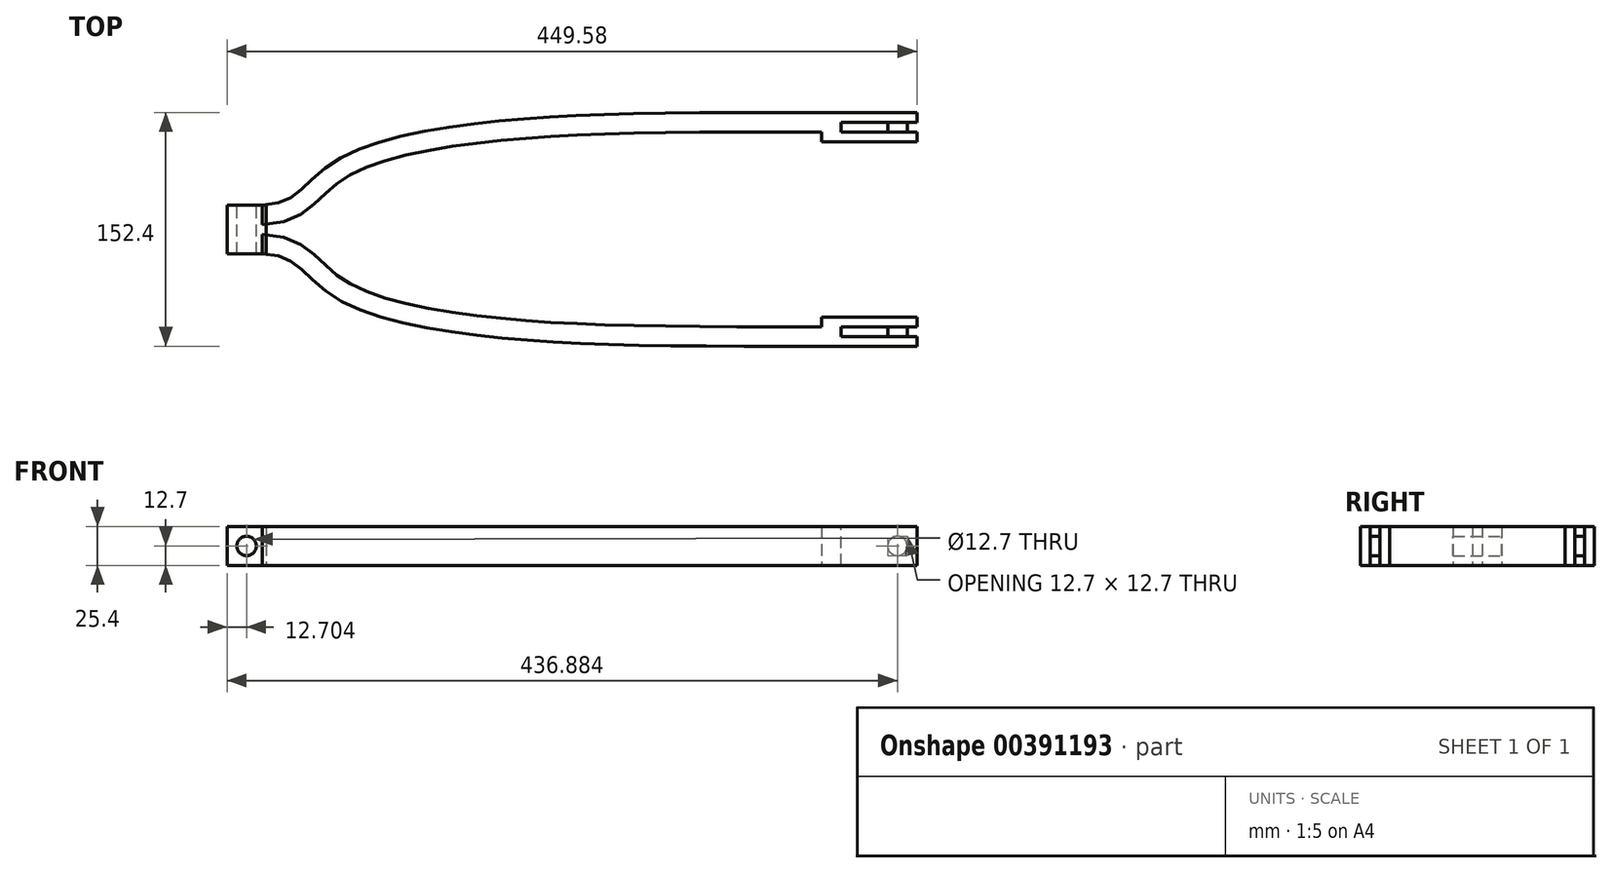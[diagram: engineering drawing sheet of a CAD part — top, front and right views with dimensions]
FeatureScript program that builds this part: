
annotation { "Feature Type Name" : "Feature", "Feature Type Description" : "" }
export const myFeature = defineFeature(function(context is Context, id is Id, definition is map)
    precondition{}
    {
        {
            var Q0;
            Q0=qCreatedBy(makeId("Top.planeOp"),FACE);
            var sketch = newSketch(context, id + "F0", { "sketchPlane" : qUnion([Q0])});
            skLineSegment(sketch, "E0", {"start": v(-147.55, 0) * mm, "end": v(274.1, 0) * mm, "construction": true});
            skFitSpline(sketch, "E1", {"points": [v(-147.55, -9.53) * mm, v(-100.59, -36.49) * mm, v(0, -63.5) * mm, v(223.3, -69.85) * mm], "startDerivative": vector(326.66, -0.96) * mm, "endDerivative": vector(713.6, 0) * mm});
            skLineSegment(sketch, "E2", {"start": v(-147.55, -185.95) * mm, "end": v(-147.55, 189.82) * mm, "construction": true});
            skFitSpline(sketch, "E3.MirrorCS", {"points": [v(-147.55, 9.53) * mm, v(-100.59, 36.49) * mm, v(0, 63.5) * mm, v(223.3, 69.85) * mm], "startDerivative": vector(326.66, 0.96) * mm, "endDerivative": vector(713.6, 0) * mm});
            skLineSegment(sketch, "E4", {"start": v(223.3, -69.85) * mm, "end": v(223.3, 69.85) * mm, "construction": true});
            skLineSegment(sketch, "E5", {"start": v(223.3, 69.85) * mm, "end": v(223.3, 69.85) * mm});
            skLineSegment(sketch, "E6", {"start": v(279.17, -108.03) * mm, "end": v(279.17, 69.85) * mm, "construction": true});
            skLineSegment(sketch, "E7", {"start": v(279.17, 57.15) * mm, "end": v(223.3, 57.15) * mm});
            skLineSegment(sketch, "E8", {"start": v(279.17, -57.15) * mm, "end": v(223.3, -57.15) * mm});
            skLineSegment(sketch, "E9", {"start": v(223.3, 69.85) * mm, "end": v(279.17, 69.85) * mm});
            skLineSegment(sketch, "E10", {"start": v(223.3, -69.85) * mm, "end": v(279.17, -69.85) * mm});
            skSolve(sketch);
        }
        {
            var Q0;
            Q0=sQuery(id+"F0.wireOp",VERTEX,"E3.MirrorCS.0.internal");
            var Q1;
            Q1=qCreatedBy(makeId("Right.planeOp"),FACE);
            cPlane(context, id + "F1", {"entities" : qUnion([Q0, Q1]), "cplaneType" : CPlaneType.PLANE_POINT, "offset" : 25.4 * mm, "width" : 152.4 * mm, "height" : 152.4 * mm});
        }
        {
            var Q0;
            Q0=qCreatedBy(id+"F1.planeOp",FACE);
            var sketch = newSketch(context, id + "F2", { "sketchPlane" : qUnion([Q0])});
            skLineSegment(sketch, "E11.bottom", {"start": v(15.88, 12.7) * mm, "end": v(3.18, 12.7) * mm});
            skLineSegment(sketch, "E11.top", {"start": v(15.88, -12.7) * mm, "end": v(3.18, -12.7) * mm});
            skLineSegment(sketch, "E11.left", {"start": v(15.88, 12.7) * mm, "end": v(15.88, -12.7) * mm});
            skLineSegment(sketch, "E11.right", {"start": v(3.18, 12.7) * mm, "end": v(3.18, -12.7) * mm});
            skPoint(sketch, "E11.middle", {"position": v(9.53, 0) * mm});
            skLineSegment(sketch, "E12.bottom", {"start": v(-3.18, 12.7) * mm, "end": v(-15.88, 12.7) * mm});
            skLineSegment(sketch, "E12.top", {"start": v(-3.18, -12.7) * mm, "end": v(-15.88, -12.7) * mm});
            skLineSegment(sketch, "E12.left", {"start": v(-3.18, 12.7) * mm, "end": v(-3.17, -12.7) * mm});
            skLineSegment(sketch, "E12.right", {"start": v(-15.88, 12.7) * mm, "end": v(-15.88, -12.7) * mm});
            skPoint(sketch, "E12.middle", {"position": v(-9.52, 0) * mm});
            skSolve(sketch);
        }
        {
            var Q0;
            Q0=makeQuery(id+"F2.imprint","IMPRINT",FACE,{"disambiguationData":[TD([[makeQuery(id+"F2.imprint","IMPRINT",EDGE,{"derivedFrom":sQuery(id+"F2.wireOp",EDGE,"E12.bottom")}),1.0]])]});
            var Q1;
            Q1=sQuery(id+"F0.wireOp",EDGE,"E1");
            sweep(context, id + "F3", {"profiles" : qUnion([Q0]), "path" : qUnion([Q1])});
        }
        {
            var Q0;
            Q0=makeQuery(id+"F2.imprint","IMPRINT",FACE,{"disambiguationData":[TD([[makeQuery(id+"F2.imprint","IMPRINT",EDGE,{"derivedFrom":sQuery(id+"F2.wireOp",EDGE,"E11.bottom")}),1.0]])]});
            var Q1;
            Q1=sQuery(id+"F0.wireOp",EDGE,"E3.MirrorCS");
            sweep(context, id + "F4", {"profiles" : qUnion([Q0]), "path" : qUnion([Q1])});
        }
        {
            var Q0;
            Q0=sQuery(id+"F0.wireOp",VERTEX,"E8.end");
            var Q1;
            Q1=qCreatedBy(makeId("Right.planeOp"),FACE);
            cPlane(context, id + "F5", {"entities" : qUnion([Q0, Q1]), "cplaneType" : CPlaneType.PLANE_POINT, "offset" : 25.4 * mm, "width" : 152.4 * mm, "height" : 152.4 * mm});
        }
        {
            var Q0;
            Q0=qCreatedBy(id+"F5.planeOp",FACE);
            var sketch = newSketch(context, id + "F6", { "sketchPlane" : qUnion([Q0])});
            skLineSegment(sketch, "E13.bottom", {"start": v(-63.5, -12.7) * mm, "end": v(-57.15, -12.7) * mm});
            skLineSegment(sketch, "E13.top", {"start": v(-63.5, 12.7) * mm, "end": v(-57.15, 12.7) * mm});
            skLineSegment(sketch, "E13.left", {"start": v(-63.5, -12.7) * mm, "end": v(-63.5, 12.7) * mm});
            skLineSegment(sketch, "E13.right", {"start": v(-57.15, -12.7) * mm, "end": v(-57.15, 12.7) * mm});
            skLineSegment(sketch, "E14.bottom", {"start": v(-76.2, 12.7) * mm, "end": v(-69.85, 12.7) * mm});
            skLineSegment(sketch, "E14.top", {"start": v(-76.2, -12.7) * mm, "end": v(-69.85, -12.7) * mm});
            skLineSegment(sketch, "E14.left", {"start": v(-76.2, 12.7) * mm, "end": v(-76.2, -12.7) * mm});
            skLineSegment(sketch, "E14.right", {"start": v(-69.85, 12.7) * mm, "end": v(-69.85, -12.7) * mm});
            skLineSegment(sketch, "E15.bottom", {"start": v(57.15, 12.7) * mm, "end": v(63.5, 12.7) * mm});
            skLineSegment(sketch, "E15.top", {"start": v(57.15, -12.7) * mm, "end": v(63.5, -12.7) * mm});
            skLineSegment(sketch, "E15.left", {"start": v(57.15, 12.7) * mm, "end": v(57.15, -12.7) * mm});
            skLineSegment(sketch, "E15.right", {"start": v(63.5, 12.7) * mm, "end": v(63.5, -12.7) * mm});
            skLineSegment(sketch, "E16.bottom", {"start": v(69.85, -12.7) * mm, "end": v(76.2, -12.7) * mm});
            skLineSegment(sketch, "E16.top", {"start": v(69.85, 12.7) * mm, "end": v(76.2, 12.7) * mm});
            skLineSegment(sketch, "E16.left", {"start": v(69.85, -12.7) * mm, "end": v(69.85, 12.7) * mm});
            skLineSegment(sketch, "E16.right", {"start": v(76.2, -12.7) * mm, "end": v(76.2, 12.7) * mm});
            skSolve(sketch);
        }
        {
            var Q0;
            Q0=makeQuery(id+"F6.imprint","IMPRINT",FACE,{"disambiguationData":[TD([[makeQuery(id+"F6.imprint","IMPRINT",EDGE,{"derivedFrom":sQuery(id+"F6.wireOp",EDGE,"E13.bottom")}),1.0]])]});
            var Q1;
            Q1=sQuery(id+"F0.wireOp",EDGE,"E8");
            sweep(context, id + "F7", {"profiles" : qUnion([Q0]), "path" : qUnion([Q1])});
        }
        {
            var Q0;
            Q0=makeQuery(id+"F6.imprint","IMPRINT",FACE,{"disambiguationData":[TD([[makeQuery(id+"F6.imprint","IMPRINT",EDGE,{"derivedFrom":sQuery(id+"F6.wireOp",EDGE,"E14.bottom")}),-1.0]])]});
            var Q1;
            Q1=sQuery(id+"F0.wireOp",EDGE,"E10");
            sweep(context, id + "F8", {"profiles" : qUnion([Q0]), "path" : qUnion([Q1])});
        }
        {
            var Q0;
            Q0=makeQuery(id+"F6.imprint","IMPRINT",FACE,{"disambiguationData":[TD([[makeQuery(id+"F6.imprint","IMPRINT",EDGE,{"derivedFrom":sQuery(id+"F6.wireOp",EDGE,"E16.bottom")}),1.0]])]});
            var Q1;
            Q1=sQuery(id+"F0.wireOp",EDGE,"E9");
            sweep(context, id + "F9", {"profiles" : qUnion([Q0]), "path" : qUnion([Q1])});
        }
        {
            var Q0;
            Q0=makeQuery(id+"F6.imprint","IMPRINT",FACE,{"disambiguationData":[TD([[makeQuery(id+"F6.imprint","IMPRINT",EDGE,{"derivedFrom":sQuery(id+"F6.wireOp",EDGE,"E15.bottom")}),-1.0]])]});
            var Q1;
            Q1=sQuery(id+"F0.wireOp",EDGE,"E7");
            sweep(context, id + "F10", {"profiles" : qUnion([Q0]), "path" : qUnion([Q1])});
        }
        {
            var Q0;
            Q0=makeQuery(id+"F4.opSweep","CAP_VERTEX",VERTEX,{"disambiguationData":[OSD([sQuery(id+"F0.wireOp",EDGE,"E3.MirrorCS"),sQuery(id+"F2.wireOp",EDGE,"E11.bottom"),sQuery(id+"F2.wireOp",EDGE,"E11.left")])],"isStart":false});
            var Q1;
            Q1=qCreatedBy(makeId("Front.planeOp"),FACE);
            cPlane(context, id + "F11", {"entities" : qUnion([Q0, Q1]), "cplaneType" : CPlaneType.PLANE_POINT, "offset" : 25.4 * mm, "width" : 152.4 * mm, "height" : 152.4 * mm});
        }
        {
            var Q0;
            Q0=qCreatedBy(id+"F11.planeOp",FACE);
            var sketch = newSketch(context, id + "F12", { "sketchPlane" : qUnion([Q0])});
            skLineSegment(sketch, "E17.bottom", {"start": v(216.94, 12.7) * mm, "end": v(223.3, 12.7) * mm});
            skLineSegment(sketch, "E17.top", {"start": v(216.94, -12.7) * mm, "end": v(229.64, -12.7) * mm});
            skLineSegment(sketch, "E17.left", {"start": v(216.94, 12.7) * mm, "end": v(216.94, -12.7) * mm});
            skLineSegment(sketch, "E17.right", {"start": v(229.64, 12.7) * mm, "end": v(229.64, -12.7) * mm});
            skLineSegment(sketch, "E18", {"start": v(223.3, 12.7) * mm, "end": v(229.64, 12.7) * mm});
            skSolve(sketch);
        }
        {
            var Q0;
            Q0=makeQuery(id+"F12.imprint","IMPRINT",FACE,{"disambiguationData":[TD([[makeQuery(id+"F12.imprint","IMPRINT",EDGE,{"derivedFrom":sQuery(id+"F12.wireOp",EDGE,"E17.bottom")}),-1.0]])]});
            extrude(context, id + "F13", {"entities" : qUnion([Q0]), "depth" : 19.05 * mm});
        }
        {
            var Q0;
            Q0=makeQuery(id+"F3.opSweep","CAP_VERTEX",VERTEX,{"disambiguationData":[OSD([sQuery(id+"F0.wireOp",EDGE,"E1"),sQuery(id+"F2.wireOp",EDGE,"E12.bottom"),sQuery(id+"F2.wireOp",EDGE,"E12.right")])],"isStart":false});
            var Q1;
            Q1=qCreatedBy(makeId("Front.planeOp"),FACE);
            cPlane(context, id + "F14", {"entities" : qUnion([Q0, Q1]), "cplaneType" : CPlaneType.PLANE_POINT, "offset" : 25.4 * mm, "width" : 152.4 * mm, "height" : 152.4 * mm});
        }
        {
            var Q0;
            Q0=qCreatedBy(id+"F14.planeOp",FACE);
            var sketch = newSketch(context, id + "F15", { "sketchPlane" : qUnion([Q0])});
            skLineSegment(sketch, "E19.bottom", {"start": v(216.94, 12.7) * mm, "end": v(223.3, 12.7) * mm});
            skLineSegment(sketch, "E19.top", {"start": v(216.94, -12.7) * mm, "end": v(229.64, -12.7) * mm});
            skLineSegment(sketch, "E19.left", {"start": v(216.94, 12.7) * mm, "end": v(216.94, -12.7) * mm});
            skLineSegment(sketch, "E19.right", {"start": v(229.64, 12.7) * mm, "end": v(229.64, -12.7) * mm});
            skLineSegment(sketch, "E20", {"start": v(223.3, 12.7) * mm, "end": v(229.64, 12.7) * mm});
            skSolve(sketch);
        }
        {
            var Q0;
            Q0=makeQuery(id+"F15.imprint","IMPRINT",FACE,{"disambiguationData":[TD([[makeQuery(id+"F15.imprint","IMPRINT",EDGE,{"derivedFrom":sQuery(id+"F15.wireOp",EDGE,"E19.bottom")}),-1.0]])]});
            extrude(context, id + "F16", {"entities" : qUnion([Q0]), "oppositeDirection" : true, "depth" : 19.05 * mm});
        }
        {
            var Q0;
            Q0=makeQuery(id+"F3.opSweep","SWEPT_BODY",BODY,{"disambiguationData":[OSD([sQuery(id+"F0.wireOp",EDGE,"E1"),sQuery(id+"F2.wireOp",EDGE,"E12.bottom"),sQuery(id+"F2.wireOp",EDGE,"E12.top"),sQuery(id+"F2.wireOp",EDGE,"E12.left"),sQuery(id+"F2.wireOp",EDGE,"E12.right")])]});
            var Q1;
            Q1=makeQuery(id+"F16.opExtrude","SWEPT_BODY",BODY,{"disambiguationData":[OSD([sQuery(id+"F15.wireOp",EDGE,"E19.bottom"),sQuery(id+"F15.wireOp",EDGE,"E19.top"),sQuery(id+"F15.wireOp",EDGE,"E19.left"),sQuery(id+"F15.wireOp",EDGE,"E19.right"),sQuery(id+"F15.wireOp",EDGE,"E20")])]});
            var Q2;
            Q2=makeQuery(id+"F8.opSweep","SWEPT_BODY",BODY,{"disambiguationData":[OSD([sQuery(id+"F0.wireOp",EDGE,"E10"),sQuery(id+"F6.wireOp",EDGE,"E14.bottom"),sQuery(id+"F6.wireOp",EDGE,"E14.top"),sQuery(id+"F6.wireOp",EDGE,"E14.left"),sQuery(id+"F6.wireOp",EDGE,"E14.right")])]});
            var Q3;
            Q3=makeQuery(id+"F7.opSweep","SWEPT_BODY",BODY,{"disambiguationData":[OSD([sQuery(id+"F0.wireOp",EDGE,"E8"),sQuery(id+"F6.wireOp",EDGE,"E13.bottom"),sQuery(id+"F6.wireOp",EDGE,"E13.top"),sQuery(id+"F6.wireOp",EDGE,"E13.left"),sQuery(id+"F6.wireOp",EDGE,"E13.right")])]});
            booleanBodies(context, id + "F17", {"operationType" : BooleanOperationType.UNION, "tools" : qUnion([Q0, Q1, Q2, Q3])});
        }
        {
            var Q0;
            Q0=makeQuery(id+"F9.opSweep","SWEPT_BODY",BODY,{"disambiguationData":[OSD([sQuery(id+"F0.wireOp",EDGE,"E9"),sQuery(id+"F6.wireOp",EDGE,"E16.bottom"),sQuery(id+"F6.wireOp",EDGE,"E16.top"),sQuery(id+"F6.wireOp",EDGE,"E16.left"),sQuery(id+"F6.wireOp",EDGE,"E16.right")])]});
            var Q1;
            Q1=makeQuery(id+"F10.opSweep","SWEPT_BODY",BODY,{"disambiguationData":[OSD([sQuery(id+"F0.wireOp",EDGE,"E7"),sQuery(id+"F6.wireOp",EDGE,"E15.bottom"),sQuery(id+"F6.wireOp",EDGE,"E15.top"),sQuery(id+"F6.wireOp",EDGE,"E15.left"),sQuery(id+"F6.wireOp",EDGE,"E15.right")])]});
            var Q2;
            Q2=makeQuery(id+"F13.opExtrude","SWEPT_BODY",BODY,{"disambiguationData":[OSD([sQuery(id+"F12.wireOp",EDGE,"E17.bottom"),sQuery(id+"F12.wireOp",EDGE,"E17.top"),sQuery(id+"F12.wireOp",EDGE,"E17.left"),sQuery(id+"F12.wireOp",EDGE,"E17.right"),sQuery(id+"F12.wireOp",EDGE,"E18")])]});
            var Q3;
            Q3=makeQuery(id+"F4.opSweep","SWEPT_BODY",BODY,{"disambiguationData":[OSD([sQuery(id+"F0.wireOp",EDGE,"E3.MirrorCS"),sQuery(id+"F2.wireOp",EDGE,"E11.bottom"),sQuery(id+"F2.wireOp",EDGE,"E11.top"),sQuery(id+"F2.wireOp",EDGE,"E11.left"),sQuery(id+"F2.wireOp",EDGE,"E11.right")])]});
            booleanBodies(context, id + "F18", {"operationType" : BooleanOperationType.UNION, "tools" : qUnion([Q0, Q1, Q2, Q3])});
        }
        {
            var Q0;
            Q0=makeQuery(id+"F8.opSweep","SWEPT_FACE",FACE,{"disambiguationData":[OSD([sQuery(id+"F0.wireOp",EDGE,"E10"),sQuery(id+"F6.wireOp",EDGE,"E14.left")])]});
            var sketch = newSketch(context, id + "F19", { "sketchPlane" : qUnion([Q0])});
            skCircle(sketch, "E21", {"center": v(266.47, 0) * mm, "radius": 6.35 * mm});
            skSolve(sketch);
        }
        {
            var Q0;
            Q0=makeQuery(id+"F19.imprint","IMPRINT",FACE,{"disambiguationData":[TD([[makeQuery(id+"F19.imprint","IMPRINT",EDGE,{"derivedFrom":sQuery(id+"F19.wireOp",EDGE,"E21")}),1.0]])]});
            extrude(context, id + "F20", {"entities" : qUnion([Q0]), "operationType" : NewBodyOperationType.ADD, "oppositeDirection" : true, "depth" : 19.05 * mm});
        }
        {
            var Q0;
            Q0=makeQuery(id+"F9.opSweep","SWEPT_FACE",FACE,{"disambiguationData":[OSD([sQuery(id+"F0.wireOp",EDGE,"E9"),sQuery(id+"F6.wireOp",EDGE,"E16.right")])]});
            var sketch = newSketch(context, id + "F21", { "sketchPlane" : qUnion([Q0])});
            skCircle(sketch, "E22", {"center": v(-266.47, 0) * mm, "radius": 6.35 * mm});
            skSolve(sketch);
        }
        {
            var Q0;
            Q0=makeQuery(id+"F21.imprint","IMPRINT",FACE,{"disambiguationData":[TD([[makeQuery(id+"F21.imprint","IMPRINT",EDGE,{"derivedFrom":sQuery(id+"F21.wireOp",EDGE,"E22")}),1.0]])]});
            extrude(context, id + "F22", {"entities" : qUnion([Q0]), "operationType" : NewBodyOperationType.ADD, "oppositeDirection" : true, "depth" : 19.05 * mm});
        }
        {
            var Q0;
            Q0=sQuery(id+"F0.wireOp",VERTEX,"E0.start");
            var Q1;
            Q1=qCreatedBy(makeId("Front.planeOp"),FACE);
            cPlane(context, id + "F23", {"entities" : qUnion([Q0, Q1]), "cplaneType" : CPlaneType.PLANE_POINT, "offset" : 25.4 * mm, "width" : 152.4 * mm, "height" : 152.4 * mm});
        }
        {
            var Q0;
            Q0=qCreatedBy(id+"F23.planeOp",FACE);
            var sketch = newSketch(context, id + "F24", { "sketchPlane" : qUnion([Q0])});
            skLineSegment(sketch, "E23.bottom", {"start": v(-170.4, 12.7) * mm, "end": v(-145, 12.7) * mm});
            skLineSegment(sketch, "E23.top", {"start": v(-170.4, -12.7) * mm, "end": v(-145, -12.7) * mm});
            skLineSegment(sketch, "E23.left", {"start": v(-170.4, 12.7) * mm, "end": v(-170.4, -12.7) * mm});
            skLineSegment(sketch, "E23.right", {"start": v(-145, 12.7) * mm, "end": v(-145, -12.7) * mm});
            skCircle(sketch, "E24", {"center": v(-157.7, 0) * mm, "radius": 6.35 * mm});
            skSolve(sketch);
        }
        {
            var Q0;
            Q0=makeQuery(id+"F24.imprint","IMPRINT",FACE,{"disambiguationData":[TD([[makeQuery(id+"F24.imprint","IMPRINT",EDGE,{"derivedFrom":sQuery(id+"F24.wireOp",EDGE,"E23.bottom")}),-1.0]])]});
            extrude(context, id + "F25", {"entities" : qUnion([Q0]), "depth" : 31.75 * mm, "symmetric" : true});
        }
    });
